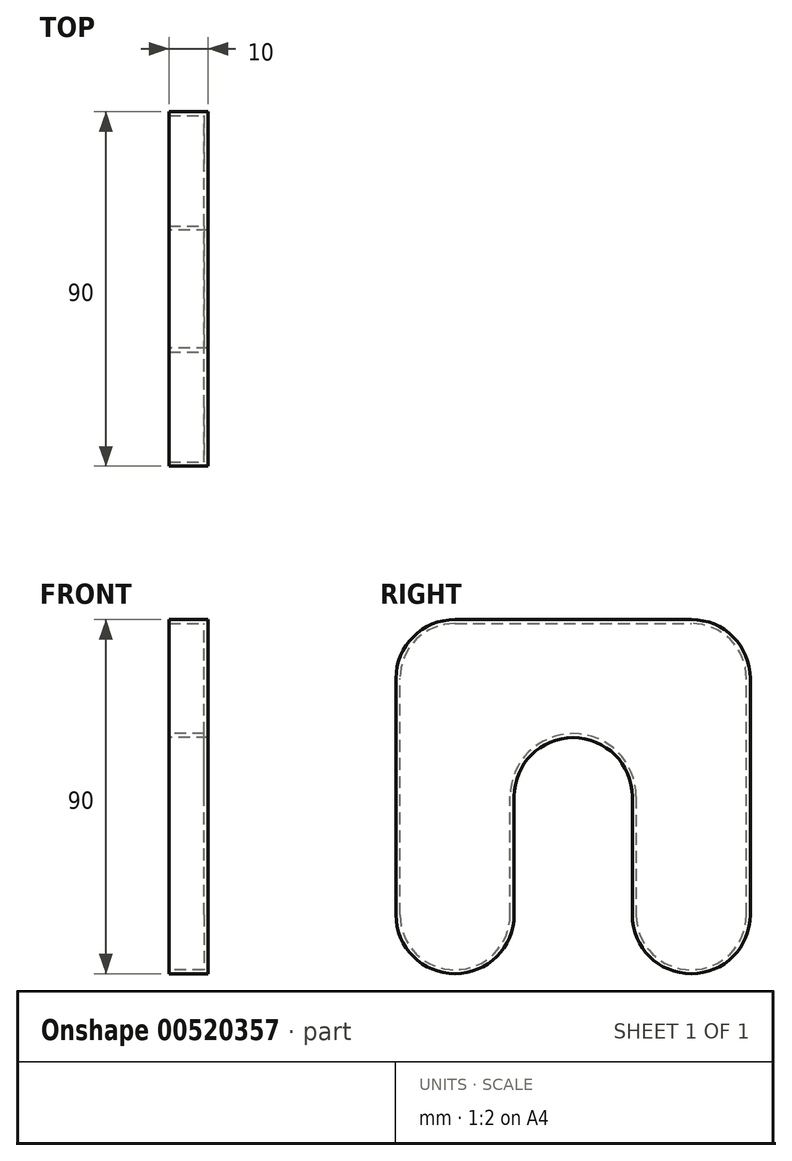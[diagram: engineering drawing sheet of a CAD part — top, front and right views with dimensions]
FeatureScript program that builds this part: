
annotation { "Feature Type Name" : "Feature", "Feature Type Description" : "" }
export const myFeature = defineFeature(function(context is Context, id is Id, definition is map)
    precondition{}
    {
        {
            var Q0;
            Q0=qCreatedBy(makeId("Right.planeOp"),FACE);
            var sketch = newSketch(context, id + "F0", { "sketchPlane" : qUnion([Q0])});
            skLineSegment(sketch, "E0.bottom", {"start": v(15, 0) * mm, "end": v(15, 0) * mm});
            skLineSegment(sketch, "E0.top", {"start": v(15, 90) * mm, "end": v(75, 90) * mm});
            skLineSegment(sketch, "E0.left", {"start": v(0, 15) * mm, "end": v(0, 75) * mm});
            skLineSegment(sketch, "E0.right", {"start": v(90, 15) * mm, "end": v(90, 75) * mm});
            skLineSegment(sketch, "E1", {"start": v(30, 15) * mm, "end": v(30, 45) * mm});
            skLineSegment(sketch, "E2", {"start": v(45, 60) * mm, "end": v(45, 60) * mm});
            skLineSegment(sketch, "E3", {"start": v(60, 45) * mm, "end": v(60, 15) * mm});
            skLineSegment(sketch, "E4.trimOffspring", {"start": v(75, 0) * mm, "end": v(75, 0) * mm});
            skPoint(sketch, "E5.visualSharp", {"position": v(0, 90) * mm});
            skArc(sketch, "E5.filletArc", {"start": v(15, 90) * mm, "mid": v(4.4, 85.6) * mm, "end": v(0, 75) * mm});
            skPoint(sketch, "E6.visualSharp", {"position": v(90, 90) * mm});
            skArc(sketch, "E6.filletArc", {"start": v(90, 75) * mm, "mid": v(85.6, 85.6) * mm, "end": v(75, 90) * mm});
            skPoint(sketch, "E7.visualSharp", {"position": v(0, 0) * mm});
            skArc(sketch, "E7.filletArc", {"start": v(0, 15) * mm, "mid": v(4.4, 4.4) * mm, "end": v(15, 0) * mm});
            skPoint(sketch, "E8.visualSharp", {"position": v(30, 0) * mm});
            skArc(sketch, "E8.filletArc", {"start": v(15, 0) * mm, "mid": v(25.6, 4.4) * mm, "end": v(30, 15) * mm});
            skPoint(sketch, "E9.visualSharp", {"position": v(60, 0) * mm});
            skArc(sketch, "E9.filletArc", {"start": v(60, 15) * mm, "mid": v(64.4, 4.4) * mm, "end": v(75, 0) * mm});
            skPoint(sketch, "E10.visualSharp", {"position": v(90, 0) * mm});
            skArc(sketch, "E10.filletArc", {"start": v(75, 0) * mm, "mid": v(85.6, 4.4) * mm, "end": v(90, 15) * mm});
            skPoint(sketch, "E11.visualSharp", {"position": v(30, 60) * mm});
            skArc(sketch, "E11.filletArc", {"start": v(45, 60) * mm, "mid": v(34.4, 55.6) * mm, "end": v(30, 45) * mm});
            skPoint(sketch, "E12.visualSharp", {"position": v(60, 60) * mm});
            skArc(sketch, "E12.filletArc", {"start": v(60, 45) * mm, "mid": v(55.6, 55.6) * mm, "end": v(45, 60) * mm});
            skSolve(sketch);
        }
        {
            var Q0;
            Q0=makeQuery(id+"F0.imprint","IMPRINT",FACE,{"disambiguationData":[TD([[makeQuery(id+"F0.imprint","IMPRINT",EDGE,{"derivedFrom":sQuery(id+"F0.wireOp",EDGE,"E0.top")}),-1.0]])]});
            extrude(context, id + "F1", {"entities" : qUnion([Q0]), "depth" : 10 * mm, "offsetDistance" : 25 * mm});
        }
        {
            var Q0;
            Q0=makeQuery(id+"F1.opExtrude","CAP_FACE",FACE,{"disambiguationData":[OSD([sQuery(id+"F0.wireOp",EDGE,"E0.top"),sQuery(id+"F0.wireOp",EDGE,"E0.left"),sQuery(id+"F0.wireOp",EDGE,"E0.right"),sQuery(id+"F0.wireOp",EDGE,"E1"),sQuery(id+"F0.wireOp",EDGE,"E3"),sQuery(id+"F0.wireOp",EDGE,"E5.filletArc"),sQuery(id+"F0.wireOp",EDGE,"E6.filletArc"),sQuery(id+"F0.wireOp",EDGE,"E7.filletArc"),sQuery(id+"F0.wireOp",EDGE,"E8.filletArc"),sQuery(id+"F0.wireOp",EDGE,"E9.filletArc"),sQuery(id+"F0.wireOp",EDGE,"E10.filletArc"),sQuery(id+"F0.wireOp",EDGE,"E11.filletArc"),sQuery(id+"F0.wireOp",EDGE,"E12.filletArc")])],"isStart":true});
            shell(context, id + "F2", {"entities" : qUnion([Q0]), "thickness" : 1 * mm});
        }
    });
